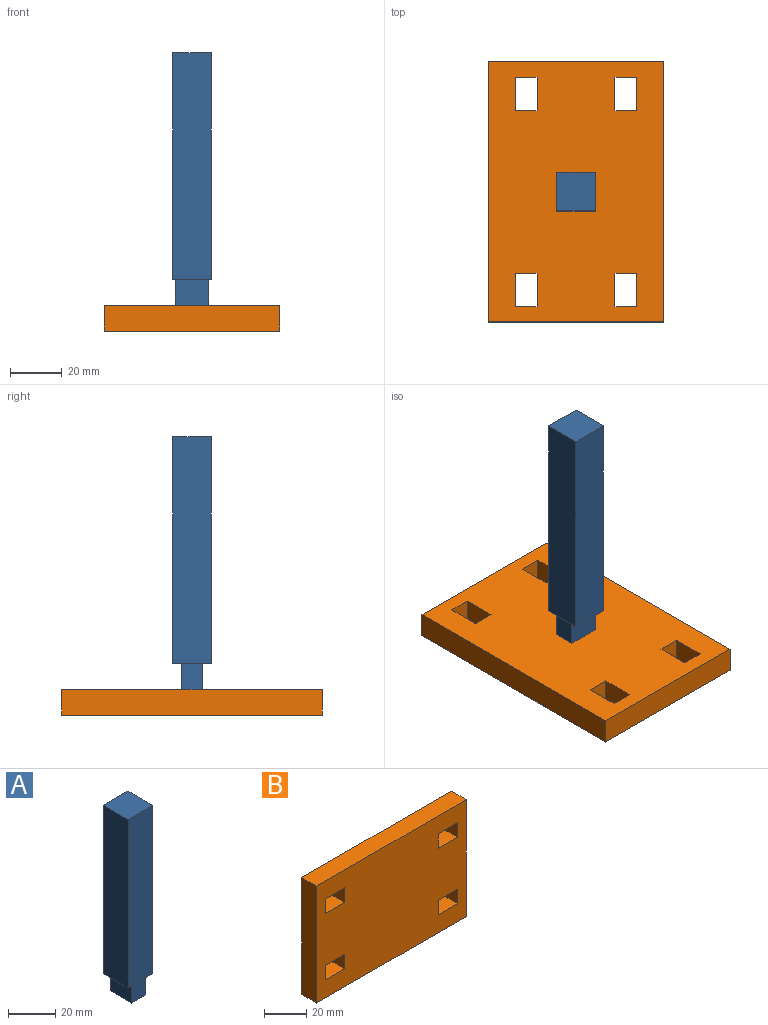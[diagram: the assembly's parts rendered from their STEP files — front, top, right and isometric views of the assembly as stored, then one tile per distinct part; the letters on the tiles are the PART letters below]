
ASSEMBLY  parts=2 mates=1
PART A: 11 faces, bbox 14.9x15x97.4 mm
  f0: plane 15x14.9mm, normal (0,0,-1), area 113.8mm2, adj f1,f3,f4,f5,f6,f7,f8,f9
  f1: plane 87.41x15mm, normal (1,0,0), area 1311.2mm2, adj f0,f2,f4,f5
  f2: plane 15x14.9mm, normal (0,0,1), area 223.5mm2, adj f1,f3,f4,f5
  f3: plane 87.41x15mm, normal (-1,0,0), area 1311.2mm2, adj f0,f2,f4,f5
  f4: plane 87.41x14.9mm, normal (0,-1,0), area 1302.2mm2, adj f0,f1,f2,f3
  f5: plane 87.41x14.9mm, normal (0,1,0), area 1302.2mm2, adj f0,f1,f2,f3
  f6: plane 13x10mm, normal (-1,0,0), area 130mm2, adj f0,f7,f9,f10
  f7: plane 10x8.45mm, normal (0,1,0), area 84.5mm2, adj f0,f6,f8,f10
  f8: plane 13x10mm, normal (1,0,0), area 130mm2, adj f0,f7,f9,f10
  f9: plane 10x8.41mm, normal (0,-1,0), area 84.1mm2, adj f0,f6,f8,f10
  f10: plane 13x8.45mm, normal (0,0,-1), area 109.6mm2, adj f6,f7,f8,f9
PART B: 22 faces, bbox 100.3x10x67.7 mm
  f0: plane 12.93x10mm, normal (0,0,-1), area 129.3mm2, adj f1,f19,f20,f21
  f1: plane 10x8.43mm, normal (-1,0,0), area 84.3mm2, adj f0,f2,f20,f21
  f2: plane 12.93x10mm, normal (0,0,1), area 129.3mm2, adj f1,f19,f20,f21
  f3: plane 10x8.43mm, normal (1,0,0), area 84.3mm2, adj f4,f15,f20,f21
  f4: plane 12.93x10mm, normal (0,0,-1), area 129.3mm2, adj f3,f5,f20,f21
  f5: plane 10x8.43mm, normal (-1,0,0), area 84.3mm2, adj f4,f15,f20,f21
  f6: plane 10x8.43mm, normal (-1,0,0), area 84.3mm2, adj f7,f16,f20,f21
  f7: plane 12.93x10mm, normal (0,0,1), area 129.3mm2, adj f6,f8,f20,f21
  f8: plane 10x8.43mm, normal (1,0,0), area 84.3mm2, adj f7,f16,f20,f21
  f9: plane 12.93x10mm, normal (0,0,1), area 129.3mm2, adj f10,f17,f20,f21
  f10: plane 10x8.43mm, normal (1,0,0), area 84.3mm2, adj f9,f11,f20,f21
  f11: plane 12.93x10mm, normal (0,0,-1), area 129.3mm2, adj f10,f17,f20,f21
  f12: plane 67.74x10mm, normal (1,0,0), area 677.4mm2, adj f13,f18,f20,f21
  f13: plane 100.34x10mm, normal (0,0,1), area 1003.4mm2, adj f12,f14,f20,f21
  f14: plane 67.74x10mm, normal (-1,0,0), area 677.4mm2, adj f13,f18,f20,f21
  f15: plane 12.93x10mm, normal (0,0,1), area 129.3mm2, adj f3,f5,f20,f21
  f16: plane 12.93x10mm, normal (0,0,-1), area 129.3mm2, adj f6,f8,f20,f21
  f17: plane 10x8.43mm, normal (-1,0,0), area 84.3mm2, adj f9,f11,f20,f21
  f18: plane 100.34x10mm, normal (0,0,-1), area 1003.4mm2, adj f12,f14,f20,f21
  f19: plane 10x8.43mm, normal (1,0,0), area 84.3mm2, adj f0,f2,f20,f21
  f20: plane 100.34x67.74mm, normal (0,-1,0), area 6361.1mm2, adj f0,f1,f2,f3,f4,f5,f6,f7
  f21: plane 100.34x67.74mm, normal (0,1,0), area 6361.1mm2, adj f0,f1,f2,f3,f4,f5,f6,f7
PLACE A rot(axis=(0,0,1),90deg) t=(-262.24,-90.59,41.12)mm
PLACE B rot(axis=(0.58,0.58,0.58),120deg) t=(-254.76,-90.56,-12.59)mm
MATE fastened A.f10 <-> B.f21  axis (0,0,-1) through (-254.76,-90.56,-12.59)mm
